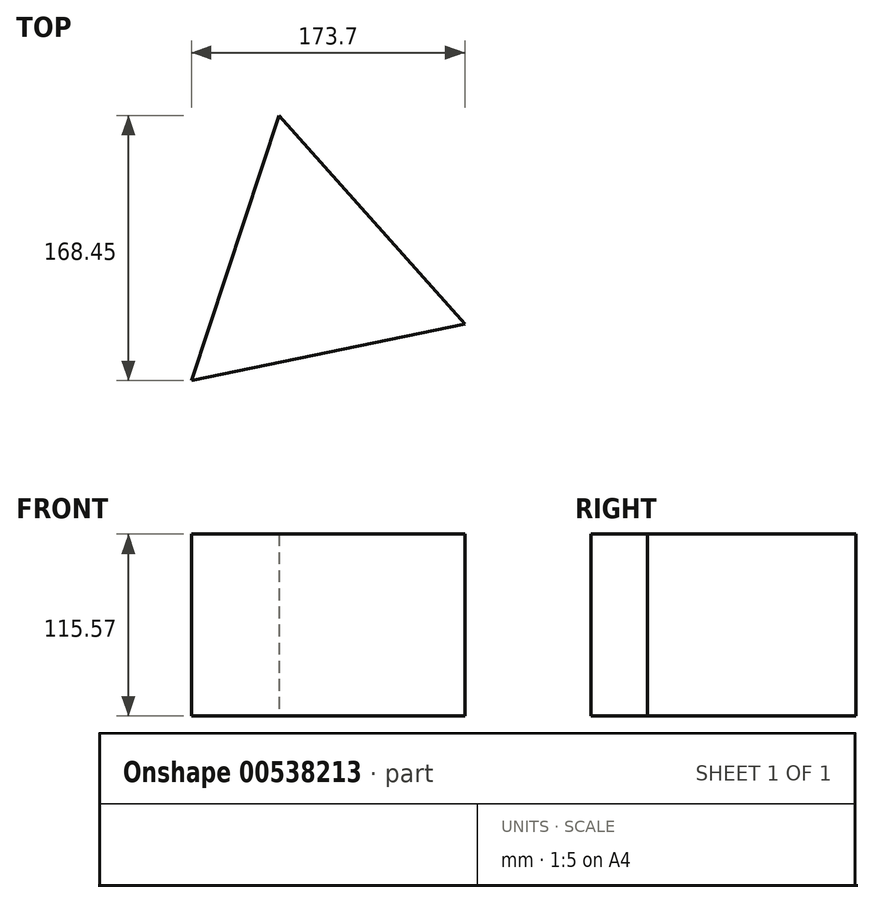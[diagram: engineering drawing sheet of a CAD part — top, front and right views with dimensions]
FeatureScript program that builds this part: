
annotation { "Feature Type Name" : "Feature", "Feature Type Description" : "" }
export const myFeature = defineFeature(function(context is Context, id is Id, definition is map)
    precondition{}
    {
        {
            var Q0;
            Q0=qCreatedBy(makeId("Top.planeOp"),FACE);
            var sketch = newSketch(context, id + "F0", { "sketchPlane" : qUnion([Q0])});
            skCircle(sketch, "E0.cCircle", {"center": v(5.96, -21.68) * mm, "radius": 51.21 * mm, "construction": true});
            skLineSegment(sketch, "E0.0", {"start": v(-14.85, 78.6) * mm, "end": v(103.22, -53.8) * mm});
            skLineSegment(sketch, "E0.1", {"start": v(103.22, -53.8) * mm, "end": v(-70.48, -89.85) * mm});
            skLineSegment(sketch, "E0.2", {"start": v(-70.48, -89.85) * mm, "end": v(-14.85, 78.6) * mm});
            skPoint(sketch, "E0.0.midPoint", {"position": v(44.19, 12.4) * mm});
            skCircle(sketch, "E1.cCircle", {"center": v(-7.71, -33.95) * mm, "radius": 30.88 * mm, "construction": true});
            skLineSegment(sketch, "E1.0", {"start": v(-0.62, 27.4) * mm, "end": v(41.87, -70.77) * mm});
            skLineSegment(sketch, "E1.1", {"start": v(41.87, -70.77) * mm, "end": v(-64.4, -58.48) * mm});
            skLineSegment(sketch, "E1.2", {"start": v(-64.4, -58.48) * mm, "end": v(-0.62, 27.4) * mm});
            skPoint(sketch, "E1.0.midPoint", {"position": v(20.63, -21.68) * mm});
            skSolve(sketch);
        }
        {
            var Q0;
            {var subQ6=sQuery(id+"F0.wireOp",EDGE,"E0.0");Q0=makeQuery(id+"F0.imprint","IMPRINT",FACE,{"disambiguationData":[TD([[makeQuery(id+"F0.imprint","IMPRINT",EDGE,{"derivedFrom":subQ6}),-1.0]])]});}
            var Q1;
            {var subQ0=sQuery(id+"F0.wireOp",EDGE,"E0.2");var subQ1=sQuery(id+"F0.wireOp",EDGE,"E0.1");var subQ2=makeQuery(id+"F0.imprint","INTERSECT",VERTEX,{"derivedFrom":[subQ1,subQ0]});Q1=makeQuery(id+"F0.imprint","IMPRINT",FACE,{"disambiguationData":[TD([[makeQuery(id+"F0.imprint","IMPRINT",EDGE,{"disambiguationData":[TD([[subQ2,1.0]])],"derivedFrom":subQ1}),-1.0]])]});}
            var Q2;
            {var subQ1=sQuery(id+"F0.wireOp",EDGE,"E0.1");var subQ7=sQuery(id+"F0.wireOp",EDGE,"E1.0");var subQ9=makeQuery(id+"F0.imprint","INTERSECT",VERTEX,{"derivedFrom":[subQ1,subQ7]});Q2=makeQuery(id+"F0.imprint","IMPRINT",FACE,{"disambiguationData":[TD([[makeQuery(id+"F0.imprint","IMPRINT",EDGE,{"disambiguationData":[TD([[subQ9,-1.0]])],"derivedFrom":subQ1}),-1.0]])]});}
            extrude(context, id + "F1", {"entities" : qUnion([Q0, Q1, Q2]), "depth" : 115.57 * mm, "offsetDistance" : 25.4 * mm});
        }
    });
